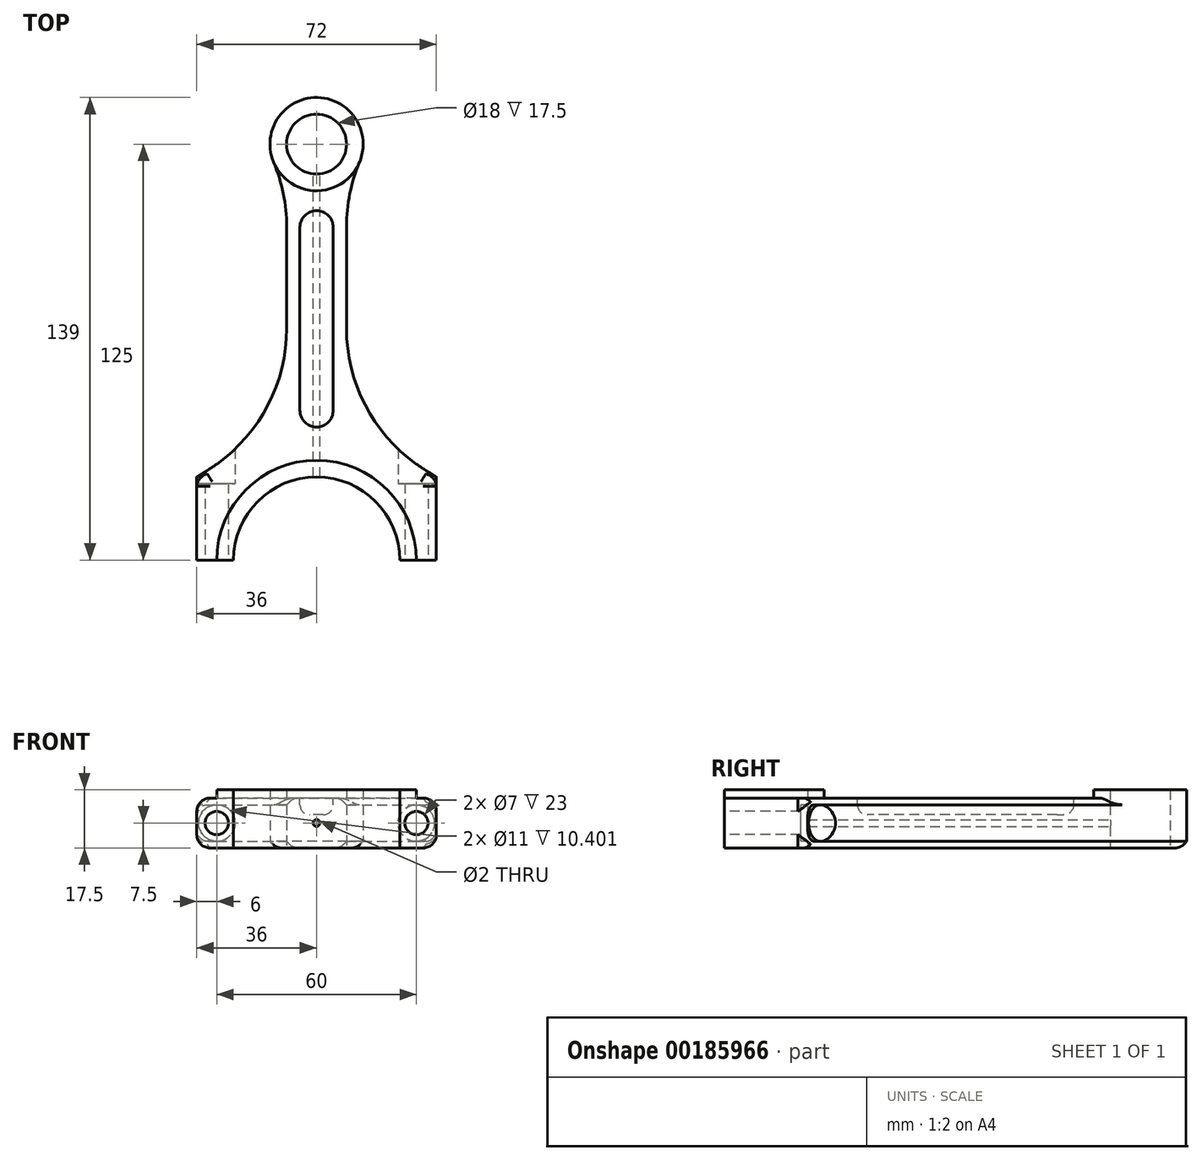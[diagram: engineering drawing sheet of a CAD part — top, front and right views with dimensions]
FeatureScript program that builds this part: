
annotation { "Feature Type Name" : "Feature", "Feature Type Description" : "" }
export const myFeature = defineFeature(function(context is Context, id is Id, definition is map)
    precondition{}
    {
        {
            var Q0;
            Q0=qCreatedBy(makeId("Top.planeOp"),FACE);
            var sketch = newSketch(context, id + "F0", { "sketchPlane" : qUnion([Q0])});
            skLineSegment(sketch, "E0", {"start": v(25, 0) * mm, "end": v(36, 0) * mm});
            skLineSegment(sketch, "E1", {"start": v(36, 0) * mm, "end": v(36, 25) * mm});
            skLineSegment(sketch, "E2", {"start": v(36, 25) * mm, "end": v(32.5, 27.19) * mm});
            skArc(sketch, "E3", {"start": v(32.5, 27.19) * mm, "mid": v(15.26, 45.35) * mm, "end": v(9, 69.59) * mm});
            skLineSegment(sketch, "E4", {"start": v(9, 69.59) * mm, "end": v(9, 100.2) * mm});
            skArc(sketch, "E5", {"start": v(9, 100.2) * mm, "mid": v(9.98, 110.08) * mm, "end": v(12.9, 119.57) * mm});
            skArc(sketch, "E6", {"start": v(12.9, 119.57) * mm, "mid": v(11.66, 132.75) * mm, "end": v(0, 139) * mm});
            skLineSegment(sketch, "E7", {"start": v(0, -25) * mm, "end": v(0, 183.63) * mm, "construction": true});
            skArc(sketch, "E8", {"start": v(25, 0) * mm, "mid": v(17.68, 17.68) * mm, "end": v(0, 25) * mm});
            skArc(sketch, "E9", {"start": v(0, 116) * mm, "mid": v(9, 125) * mm, "end": v(0, 134) * mm});
            skLineSegment(sketch, "E10.MirrorCS", {"start": v(-36, 25) * mm, "end": v(-32.5, 27.19) * mm});
            skLineSegment(sketch, "E11.MirrorCS", {"start": v(-36, 0) * mm, "end": v(-36, 25) * mm});
            skArc(sketch, "E12.MirrorCS", {"start": v(0, 116) * mm, "mid": v(-9, 125) * mm, "end": v(0, 134) * mm});
            skArc(sketch, "E13.MirrorCS", {"start": v(-25, 0) * mm, "mid": v(-17.68, 17.68) * mm, "end": v(0, 25) * mm});
            skArc(sketch, "E14.MirrorCS", {"start": v(-32.5, 27.19) * mm, "mid": v(-15.26, 45.35) * mm, "end": v(-9, 69.59) * mm});
            skLineSegment(sketch, "E15.MirrorCS", {"start": v(-25, 0) * mm, "end": v(-36, 0) * mm});
            skLineSegment(sketch, "E16.MirrorCS", {"start": v(-9, 69.59) * mm, "end": v(-9, 100.2) * mm});
            skArc(sketch, "E17.MirrorCS", {"start": v(-9, 100.2) * mm, "mid": v(-9.98, 110.08) * mm, "end": v(-12.9, 119.57) * mm});
            skArc(sketch, "E18.MirrorCS", {"start": v(-12.9, 119.57) * mm, "mid": v(-11.66, 132.75) * mm, "end": v(0, 139) * mm});
            skSolve(sketch);
        }
        {
            var Q0;
            Q0 = qSketchRegion(id + "F0", true);
            extrude(context, id + "F1", {"entities" : qUnion([Q0]), "depth" : 15 * mm, "symmetric" : true});
        }
        {
            var Q0;
            Q0=makeQuery(id+"F1.opExtrude","CAP_FACE",FACE,{"disambiguationData":[OSD([sQuery(id+"F0.wireOp",EDGE,"E0"),sQuery(id+"F0.wireOp",EDGE,"E1"),sQuery(id+"F0.wireOp",EDGE,"E2"),sQuery(id+"F0.wireOp",EDGE,"E3"),sQuery(id+"F0.wireOp",EDGE,"E4"),sQuery(id+"F0.wireOp",EDGE,"E5"),sQuery(id+"F0.wireOp",EDGE,"E6"),sQuery(id+"F0.wireOp",EDGE,"E8"),sQuery(id+"F0.wireOp",EDGE,"E9"),sQuery(id+"F0.wireOp",EDGE,"E10.MirrorCS"),sQuery(id+"F0.wireOp",EDGE,"E11.MirrorCS"),sQuery(id+"F0.wireOp",EDGE,"E12.MirrorCS"),sQuery(id+"F0.wireOp",EDGE,"E13.MirrorCS"),sQuery(id+"F0.wireOp",EDGE,"E14.MirrorCS"),sQuery(id+"F0.wireOp",EDGE,"E15.MirrorCS"),sQuery(id+"F0.wireOp",EDGE,"E16.MirrorCS"),sQuery(id+"F0.wireOp",EDGE,"E17.MirrorCS"),sQuery(id+"F0.wireOp",EDGE,"E18.MirrorCS")])],"isStart":false});
            var sketch = newSketch(context, id + "F2", { "sketchPlane" : qUnion([Q0])});
            skArc(sketch, "E19", {"start": v(30, 0) * mm, "mid": v(0, 30) * mm, "end": v(-30, 0) * mm});
            skCircle(sketch, "E20", {"center": v(0, 125) * mm, "radius": 14 * mm});
            skLineSegment(sketch, "E21", {"start": v(-30, 0) * mm, "end": v(30, 0) * mm});
            skSolve(sketch);
        }
        {
            var Q0;
            Q0=makeQuery(id+"F2.imprint","IMPRINT",FACE,{"disambiguationData":[TD([[makeQuery(id+"F2.imprint","IMPRINT",EDGE,{"derivedFrom":makeQuery(id+"F1.opExtrude","CAP_EDGE",EDGE,{"disambiguationData":[OSD([sQuery(id+"F0.wireOp",EDGE,"E9"),sQuery(id+"F0.wireOp",EDGE,"E12.MirrorCS")])],"isStart":false})}),-1.0]])]});
            var Q1;
            {var subQ0=sQuery(id+"F2.wireOp",EDGE,"E19");Q1=makeQuery(id+"F2.imprint","IMPRINT",FACE,{"disambiguationData":[TD([[makeQuery(id+"F2.imprint","IMPRINT",EDGE,{"derivedFrom":subQ0}),1.0]])]});}
            extrude(context, id + "F3", {"entities" : qUnion([Q0, Q1]), "operationType" : NewBodyOperationType.ADD, "depth" : 2.5 * mm});
        }
        {
            var Q0;
            Q0=makeQuery(id+"F1.opExtrude","CAP_FACE",FACE,{"disambiguationData":[OSD([sQuery(id+"F0.wireOp",EDGE,"E0"),sQuery(id+"F0.wireOp",EDGE,"E1"),sQuery(id+"F0.wireOp",EDGE,"E2"),sQuery(id+"F0.wireOp",EDGE,"E3"),sQuery(id+"F0.wireOp",EDGE,"E4"),sQuery(id+"F0.wireOp",EDGE,"E5"),sQuery(id+"F0.wireOp",EDGE,"E6"),sQuery(id+"F0.wireOp",EDGE,"E8"),sQuery(id+"F0.wireOp",EDGE,"E9"),sQuery(id+"F0.wireOp",EDGE,"E10.MirrorCS"),sQuery(id+"F0.wireOp",EDGE,"E11.MirrorCS"),sQuery(id+"F0.wireOp",EDGE,"E12.MirrorCS"),sQuery(id+"F0.wireOp",EDGE,"E13.MirrorCS"),sQuery(id+"F0.wireOp",EDGE,"E14.MirrorCS"),sQuery(id+"F0.wireOp",EDGE,"E15.MirrorCS"),sQuery(id+"F0.wireOp",EDGE,"E16.MirrorCS"),sQuery(id+"F0.wireOp",EDGE,"E17.MirrorCS"),sQuery(id+"F0.wireOp",EDGE,"E18.MirrorCS")])],"isStart":false});
            var sketch = newSketch(context, id + "F4", { "sketchPlane" : qUnion([Q0])});
            skLineSegment(sketch, "E22.left", {"start": v(5, 100) * mm, "end": v(5, 45) * mm});
            skLineSegment(sketch, "E22.right", {"start": v(-5, 100) * mm, "end": v(-5, 45) * mm});
            skPoint(sketch, "E22.middle", {"position": v(0, 72.5) * mm});
            skArc(sketch, "E23", {"start": v(-5, 100) * mm, "mid": v(0, 105) * mm, "end": v(5, 100) * mm});
            skArc(sketch, "E24", {"start": v(-5, 45) * mm, "mid": v(0, 40) * mm, "end": v(5, 45) * mm});
            skSolve(sketch);
        }
        {
            var Q0;
            Q0 = qSketchRegion(id + "F4", true);
            extrude(context, id + "F5", {"entities" : qUnion([Q0]), "operationType" : NewBodyOperationType.REMOVE, "oppositeDirection" : true, "depth" : 5 * mm});
        }
        {
            var Q0;
            Q0=makeQuery(id+"F1.opExtrude","CAP_EDGE",EDGE,{"disambiguationData":[OSD([sQuery(id+"F0.wireOp",EDGE,"E3")])],"isStart":false});
            var Q1;
            Q1=makeQuery(id+"F1.opExtrude","CAP_EDGE",EDGE,{"disambiguationData":[OSD([sQuery(id+"F0.wireOp",EDGE,"E3")])],"isStart":true});
            var Q2;
            Q2=makeQuery(id+"F1.opExtrude","CAP_EDGE",EDGE,{"disambiguationData":[OSD([sQuery(id+"F0.wireOp",EDGE,"E14.MirrorCS")])],"isStart":false});
            var Q3;
            Q3=makeQuery(id+"F1.opExtrude","CAP_EDGE",EDGE,{"disambiguationData":[OSD([sQuery(id+"F0.wireOp",EDGE,"E14.MirrorCS")])],"isStart":true});
            chamfer(context, id + "F6", {"entities" : qUnion([Q0, Q1, Q2, Q3]), "width" : 2 * mm, "tangentPropagation" : true});
        }
        {
            var Q0;
            {var subQ0=sQuery(id+"F2.wireOp",EDGE,"E21");var subQ1=sQuery(id+"F0.wireOp",EDGE,"E15.MirrorCS");var subQ2=makeQuery(id+"F2.imprint","IMPRINT",EDGE,{"disambiguationData":[TD([[makeQuery(id+"F2.imprint","INTERSECT",VERTEX,{"derivedFrom":[makeQuery(id+"F1.opExtrude","CAP_EDGE",EDGE,{"disambiguationData":[OSD([subQ1])],"isStart":false}),sQuery(id+"F2.wireOp",EDGE,"E19"),subQ0]}),1.0]])],"derivedFrom":subQ0});Q0=makeQuery(id+"FnDwNdTiISAMKlj_1.1.F3.boolean.opBoolean","MERGE",FACE,{"derivedFrom":[makeQuery(id+"F3.boolean.opBoolean","MERGE",FACE,{"derivedFrom":[makeQuery(id+"F1.opExtrude","SWEPT_FACE",FACE,{"disambiguationData":[OSD([subQ1])]}),makeQuery(id+"F3.opExtrude","SWEPT_FACE",FACE,{"disambiguationData":[OSD([subQ0]),TDD([subQ2])]})]}),makeQuery(id+"FnDwNdTiISAMKlj_1.1.F3.opExtrude","SWEPT_FACE",FACE,{"disambiguationData":[OSD([subQ0]),TDD([subQ2])]})]});}
            cPlane(context, id + "F7", {"entities" : qUnion([Q0]), "cplaneType" : CPlaneType.OFFSET, "offset" : 25 * mm, "oppositeDirection" : true, "width" : 150 * mm, "height" : 150 * mm});
        }
        {
            var Q0;
            Q0=qCreatedBy(id+"F7.planeOp",FACE);
            var sketch = newSketch(context, id + "F8", { "sketchPlane" : qUnion([Q0])});
            skPoint(sketch, "E25", {"position": v(-30, 0) * mm});
            skLineSegment(sketch, "E26", {"start": v(0, 28.75) * mm, "end": v(0, -30.74) * mm, "construction": true});
            skPoint(sketch, "E27.MirrorP", {"position": v(30, 0) * mm});
            skSolve(sketch);
        }
        {
            var Q0;
            Q0=sQuery(id+"F8.wireOp",VERTEX,"E27.MirrorP");
            var Q1;
            Q1=sQuery(id+"F8.wireOp",VERTEX,"E25");
            var Q2;
            Q2=makeQuery(id+"F1.opExtrude","SWEPT_BODY",BODY,{"disambiguationData":[OSD([sQuery(id+"F0.wireOp",EDGE,"E0"),sQuery(id+"F0.wireOp",EDGE,"E1"),sQuery(id+"F0.wireOp",EDGE,"E2"),sQuery(id+"F0.wireOp",EDGE,"E3"),sQuery(id+"F0.wireOp",EDGE,"E4"),sQuery(id+"F0.wireOp",EDGE,"E5"),sQuery(id+"F0.wireOp",EDGE,"E6"),sQuery(id+"F0.wireOp",EDGE,"E8"),sQuery(id+"F0.wireOp",EDGE,"E9"),sQuery(id+"F0.wireOp",EDGE,"E10.MirrorCS"),sQuery(id+"F0.wireOp",EDGE,"E11.MirrorCS"),sQuery(id+"F0.wireOp",EDGE,"E12.MirrorCS"),sQuery(id+"F0.wireOp",EDGE,"E13.MirrorCS"),sQuery(id+"F0.wireOp",EDGE,"E14.MirrorCS"),sQuery(id+"F0.wireOp",EDGE,"E15.MirrorCS"),sQuery(id+"F0.wireOp",EDGE,"E16.MirrorCS"),sQuery(id+"F0.wireOp",EDGE,"E17.MirrorCS"),sQuery(id+"F0.wireOp",EDGE,"E18.MirrorCS")])]});
            hole(context, id + "F9", {"style" : HoleStyle.C_BORE, "endStyle" : HoleEndStyle.THROUGH, "oppositeDirection" : true, "holeDiameter" : 7 * mm, "cBoreDiameter" : 11 * mm, "cBoreDepth" : 2 * mm, "locations" : qUnion([Q0, Q1]), "scope" : qUnion([Q2]), "isTappedThrough" : true, "startStyle" : HoleStartStyle.SKETCH});
        }
        {
            var Q0;
            Q0=qCreatedBy(id+"F7.planeOp",FACE);
            var sketch = newSketch(context, id + "F10", { "sketchPlane" : qUnion([Q0])});
            skCircle(sketch, "E28", {"center": v(-30, 0) * mm, "radius": 5.5 * mm});
            skCircle(sketch, "E29", {"center": v(30, 0) * mm, "radius": 5.5 * mm});
            skSolve(sketch);
        }
        {
            var Q0;
            Q0 = qSketchRegion(id + "F10", true);
            extrude(context, id + "F11", {"entities" : qUnion([Q0]), "operationType" : NewBodyOperationType.REMOVE, "oppositeDirection" : true, "depth" : 25 * mm});
        }
        {
            var Q0;
            Q0=makeQuery(id+"F9rkkF7bLStw4Ax_1.1.F5.boolean.opBoolean","COPY",EDGE,{"derivedFrom":makeQuery(id+"F9rkkF7bLStw4Ax_1.1.F5.opExtrude","CAP_EDGE",EDGE,{"disambiguationData":[OSD([sQuery(id+"F4.wireOp",EDGE,"E22.right")])],"isStart":false})});
            var Q1;
            Q1=makeQuery(id+"FnDwNdTiISAMKlj_1.1.F3.opExtrude","CAP_EDGE",EDGE,{"disambiguationData":[OSD([sQuery(id+"F2.wireOp",EDGE,"E19")])],"isStart":true});
            var Q2;
            Q2=makeQuery(id+"F3.opExtrude","CAP_EDGE",EDGE,{"disambiguationData":[OSD([sQuery(id+"F2.wireOp",EDGE,"E19")])],"isStart":true});
            var Q3;
            Q3=makeQuery(id+"F5.boolean.opBoolean","COPY",EDGE,{"derivedFrom":makeQuery(id+"F5.opExtrude","CAP_EDGE",EDGE,{"disambiguationData":[OSD([sQuery(id+"F4.wireOp",EDGE,"E22.right")])],"isStart":false})});
            fillet(context, id + "F12", {"entities" : qUnion([Q0, Q1, Q2, Q3]), "radius" : 3 * mm, "tangentPropagation" : true, "allowEdgeOverflow" : false});
        }
        {
            var Q0;
            Q0=makeQuery(id+"F6.opChamfer","BLEND_EDGE",EDGE,{"blendedFrom":[makeQuery(id+"F1.opExtrude","CAP_EDGE",EDGE,{"disambiguationData":[OSD([sQuery(id+"F0.wireOp",EDGE,"E2")])],"isStart":true}),makeQuery(id+"F1.opExtrude","SWEPT_FACE",FACE,{"disambiguationData":[OSD([sQuery(id+"F0.wireOp",EDGE,"E1")])]})],"blendedInto":[makeQuery(id+"F1.opExtrude","SWEPT_FACE",FACE,{"disambiguationData":[OSD([sQuery(id+"F0.wireOp",EDGE,"E1")])]})]});
            var Q1;
            Q1=makeQuery(id+"F6.opChamfer","BLEND_EDGE",EDGE,{"blendedFrom":[makeQuery(id+"F1.opExtrude","CAP_EDGE",EDGE,{"disambiguationData":[OSD([sQuery(id+"F0.wireOp",EDGE,"E2")])],"isStart":false}),makeQuery(id+"F1.opExtrude","SWEPT_FACE",FACE,{"disambiguationData":[OSD([sQuery(id+"F0.wireOp",EDGE,"E1")])]})],"blendedInto":[makeQuery(id+"F1.opExtrude","SWEPT_FACE",FACE,{"disambiguationData":[OSD([sQuery(id+"F0.wireOp",EDGE,"E1")])]})]});
            var Q2;
            Q2=makeQuery(id+"F6.opChamfer","BLEND_EDGE",EDGE,{"blendedFrom":[makeQuery(id+"F1.opExtrude","CAP_EDGE",EDGE,{"disambiguationData":[OSD([sQuery(id+"F0.wireOp",EDGE,"E10.MirrorCS")])],"isStart":true}),makeQuery(id+"F1.opExtrude","SWEPT_FACE",FACE,{"disambiguationData":[OSD([sQuery(id+"F0.wireOp",EDGE,"E11.MirrorCS")])]})],"blendedInto":[makeQuery(id+"F1.opExtrude","SWEPT_FACE",FACE,{"disambiguationData":[OSD([sQuery(id+"F0.wireOp",EDGE,"E11.MirrorCS")])]})]});
            var Q3;
            Q3=makeQuery(id+"F6.opChamfer","BLEND_EDGE",EDGE,{"blendedFrom":[makeQuery(id+"F1.opExtrude","CAP_EDGE",EDGE,{"disambiguationData":[OSD([sQuery(id+"F0.wireOp",EDGE,"E10.MirrorCS")])],"isStart":false}),makeQuery(id+"F1.opExtrude","SWEPT_FACE",FACE,{"disambiguationData":[OSD([sQuery(id+"F0.wireOp",EDGE,"E11.MirrorCS")])]})],"blendedInto":[makeQuery(id+"F1.opExtrude","SWEPT_FACE",FACE,{"disambiguationData":[OSD([sQuery(id+"F0.wireOp",EDGE,"E11.MirrorCS")])]})]});
            fillet(context, id + "F13", {"entities" : qUnion([Q0, Q1, Q2, Q3]), "radius" : 5 * mm, "tangentPropagation" : true, "allowEdgeOverflow" : false});
        }
        {
            var Q0;
            {var subQ0=sQuery(id+"F0.wireOp",EDGE,"E2");var subQ1=sQuery(id+"F0.wireOp",EDGE,"E1");Q0=makeQuery(id+"F13.opFillet","BLEND_EDGE",EDGE,{"blendedFrom":[makeQuery(id+"F6.opChamfer","BLEND_EDGE",EDGE,{"blendedFrom":[makeQuery(id+"F1.opExtrude","CAP_EDGE",EDGE,{"disambiguationData":[OSD([subQ0])],"isStart":true}),makeQuery(id+"F1.opExtrude","SWEPT_FACE",FACE,{"disambiguationData":[OSD([subQ1])]})],"blendedInto":[makeQuery(id+"F1.opExtrude","SWEPT_FACE",FACE,{"disambiguationData":[OSD([subQ1])]})]}),makeQuery(id+"F1.opExtrude","CAP_FACE",FACE,{"disambiguationData":[OSD([sQuery(id+"F0.wireOp",EDGE,"E0"),subQ1,subQ0,sQuery(id+"F0.wireOp",EDGE,"E3"),sQuery(id+"F0.wireOp",EDGE,"E4"),sQuery(id+"F0.wireOp",EDGE,"E5"),sQuery(id+"F0.wireOp",EDGE,"E6"),sQuery(id+"F0.wireOp",EDGE,"E8"),sQuery(id+"F0.wireOp",EDGE,"E9"),sQuery(id+"F0.wireOp",EDGE,"E10.MirrorCS"),sQuery(id+"F0.wireOp",EDGE,"E11.MirrorCS"),sQuery(id+"F0.wireOp",EDGE,"E12.MirrorCS"),sQuery(id+"F0.wireOp",EDGE,"E13.MirrorCS"),sQuery(id+"F0.wireOp",EDGE,"E14.MirrorCS"),sQuery(id+"F0.wireOp",EDGE,"E15.MirrorCS"),sQuery(id+"F0.wireOp",EDGE,"E16.MirrorCS"),sQuery(id+"F0.wireOp",EDGE,"E17.MirrorCS"),sQuery(id+"F0.wireOp",EDGE,"E18.MirrorCS")])],"isStart":true})],"blendedInto":[makeQuery(id+"F1.opExtrude","CAP_FACE",FACE,{"disambiguationData":[OSD([sQuery(id+"F0.wireOp",EDGE,"E0"),subQ1,subQ0,sQuery(id+"F0.wireOp",EDGE,"E3"),sQuery(id+"F0.wireOp",EDGE,"E4"),sQuery(id+"F0.wireOp",EDGE,"E5"),sQuery(id+"F0.wireOp",EDGE,"E6"),sQuery(id+"F0.wireOp",EDGE,"E8"),sQuery(id+"F0.wireOp",EDGE,"E9"),sQuery(id+"F0.wireOp",EDGE,"E10.MirrorCS"),sQuery(id+"F0.wireOp",EDGE,"E11.MirrorCS"),sQuery(id+"F0.wireOp",EDGE,"E12.MirrorCS"),sQuery(id+"F0.wireOp",EDGE,"E13.MirrorCS"),sQuery(id+"F0.wireOp",EDGE,"E14.MirrorCS"),sQuery(id+"F0.wireOp",EDGE,"E15.MirrorCS"),sQuery(id+"F0.wireOp",EDGE,"E16.MirrorCS"),sQuery(id+"F0.wireOp",EDGE,"E17.MirrorCS"),sQuery(id+"F0.wireOp",EDGE,"E18.MirrorCS")])],"isStart":true})]});}
            var Q1;
            {var subQ0=sQuery(id+"F0.wireOp",EDGE,"E11.MirrorCS");var subQ1=sQuery(id+"F0.wireOp",EDGE,"E10.MirrorCS");Q1=makeQuery(id+"F13.opFillet","BLEND_EDGE",EDGE,{"blendedFrom":[makeQuery(id+"F6.opChamfer","BLEND_EDGE",EDGE,{"blendedFrom":[makeQuery(id+"F1.opExtrude","CAP_EDGE",EDGE,{"disambiguationData":[OSD([subQ1])],"isStart":true}),makeQuery(id+"F1.opExtrude","SWEPT_FACE",FACE,{"disambiguationData":[OSD([subQ0])]})],"blendedInto":[makeQuery(id+"F1.opExtrude","SWEPT_FACE",FACE,{"disambiguationData":[OSD([subQ0])]})]}),makeQuery(id+"F1.opExtrude","CAP_FACE",FACE,{"disambiguationData":[OSD([sQuery(id+"F0.wireOp",EDGE,"E0"),sQuery(id+"F0.wireOp",EDGE,"E1"),sQuery(id+"F0.wireOp",EDGE,"E2"),sQuery(id+"F0.wireOp",EDGE,"E3"),sQuery(id+"F0.wireOp",EDGE,"E4"),sQuery(id+"F0.wireOp",EDGE,"E5"),sQuery(id+"F0.wireOp",EDGE,"E6"),sQuery(id+"F0.wireOp",EDGE,"E8"),sQuery(id+"F0.wireOp",EDGE,"E9"),subQ1,subQ0,sQuery(id+"F0.wireOp",EDGE,"E12.MirrorCS"),sQuery(id+"F0.wireOp",EDGE,"E13.MirrorCS"),sQuery(id+"F0.wireOp",EDGE,"E14.MirrorCS"),sQuery(id+"F0.wireOp",EDGE,"E15.MirrorCS"),sQuery(id+"F0.wireOp",EDGE,"E16.MirrorCS"),sQuery(id+"F0.wireOp",EDGE,"E17.MirrorCS"),sQuery(id+"F0.wireOp",EDGE,"E18.MirrorCS")])],"isStart":true})],"blendedInto":[makeQuery(id+"F1.opExtrude","CAP_FACE",FACE,{"disambiguationData":[OSD([sQuery(id+"F0.wireOp",EDGE,"E0"),sQuery(id+"F0.wireOp",EDGE,"E1"),sQuery(id+"F0.wireOp",EDGE,"E2"),sQuery(id+"F0.wireOp",EDGE,"E3"),sQuery(id+"F0.wireOp",EDGE,"E4"),sQuery(id+"F0.wireOp",EDGE,"E5"),sQuery(id+"F0.wireOp",EDGE,"E6"),sQuery(id+"F0.wireOp",EDGE,"E8"),sQuery(id+"F0.wireOp",EDGE,"E9"),subQ1,subQ0,sQuery(id+"F0.wireOp",EDGE,"E12.MirrorCS"),sQuery(id+"F0.wireOp",EDGE,"E13.MirrorCS"),sQuery(id+"F0.wireOp",EDGE,"E14.MirrorCS"),sQuery(id+"F0.wireOp",EDGE,"E15.MirrorCS"),sQuery(id+"F0.wireOp",EDGE,"E16.MirrorCS"),sQuery(id+"F0.wireOp",EDGE,"E17.MirrorCS"),sQuery(id+"F0.wireOp",EDGE,"E18.MirrorCS")])],"isStart":true})]});}
            var Q2;
            {var subQ0=sQuery(id+"F0.wireOp",EDGE,"E11.MirrorCS");var subQ1=sQuery(id+"F0.wireOp",EDGE,"E10.MirrorCS");Q2=makeQuery(id+"F13.opFillet","BLEND_EDGE",EDGE,{"blendedFrom":[makeQuery(id+"F6.opChamfer","BLEND_EDGE",EDGE,{"blendedFrom":[makeQuery(id+"F1.opExtrude","CAP_EDGE",EDGE,{"disambiguationData":[OSD([subQ1])],"isStart":false}),makeQuery(id+"F1.opExtrude","SWEPT_FACE",FACE,{"disambiguationData":[OSD([subQ0])]})],"blendedInto":[makeQuery(id+"F1.opExtrude","SWEPT_FACE",FACE,{"disambiguationData":[OSD([subQ0])]})]}),makeQuery(id+"F1.opExtrude","CAP_FACE",FACE,{"disambiguationData":[OSD([sQuery(id+"F0.wireOp",EDGE,"E0"),sQuery(id+"F0.wireOp",EDGE,"E1"),sQuery(id+"F0.wireOp",EDGE,"E2"),sQuery(id+"F0.wireOp",EDGE,"E3"),sQuery(id+"F0.wireOp",EDGE,"E4"),sQuery(id+"F0.wireOp",EDGE,"E5"),sQuery(id+"F0.wireOp",EDGE,"E6"),sQuery(id+"F0.wireOp",EDGE,"E8"),sQuery(id+"F0.wireOp",EDGE,"E9"),subQ1,subQ0,sQuery(id+"F0.wireOp",EDGE,"E12.MirrorCS"),sQuery(id+"F0.wireOp",EDGE,"E13.MirrorCS"),sQuery(id+"F0.wireOp",EDGE,"E14.MirrorCS"),sQuery(id+"F0.wireOp",EDGE,"E15.MirrorCS"),sQuery(id+"F0.wireOp",EDGE,"E16.MirrorCS"),sQuery(id+"F0.wireOp",EDGE,"E17.MirrorCS"),sQuery(id+"F0.wireOp",EDGE,"E18.MirrorCS")])],"isStart":false})],"blendedInto":[makeQuery(id+"F1.opExtrude","CAP_FACE",FACE,{"disambiguationData":[OSD([sQuery(id+"F0.wireOp",EDGE,"E0"),sQuery(id+"F0.wireOp",EDGE,"E1"),sQuery(id+"F0.wireOp",EDGE,"E2"),sQuery(id+"F0.wireOp",EDGE,"E3"),sQuery(id+"F0.wireOp",EDGE,"E4"),sQuery(id+"F0.wireOp",EDGE,"E5"),sQuery(id+"F0.wireOp",EDGE,"E6"),sQuery(id+"F0.wireOp",EDGE,"E8"),sQuery(id+"F0.wireOp",EDGE,"E9"),subQ1,subQ0,sQuery(id+"F0.wireOp",EDGE,"E12.MirrorCS"),sQuery(id+"F0.wireOp",EDGE,"E13.MirrorCS"),sQuery(id+"F0.wireOp",EDGE,"E14.MirrorCS"),sQuery(id+"F0.wireOp",EDGE,"E15.MirrorCS"),sQuery(id+"F0.wireOp",EDGE,"E16.MirrorCS"),sQuery(id+"F0.wireOp",EDGE,"E17.MirrorCS"),sQuery(id+"F0.wireOp",EDGE,"E18.MirrorCS")])],"isStart":false})]});}
            var Q3;
            {var subQ0=sQuery(id+"F0.wireOp",EDGE,"E2");var subQ1=sQuery(id+"F0.wireOp",EDGE,"E1");Q3=makeQuery(id+"F13.opFillet","BLEND_EDGE",EDGE,{"blendedFrom":[makeQuery(id+"F6.opChamfer","BLEND_EDGE",EDGE,{"blendedFrom":[makeQuery(id+"F1.opExtrude","CAP_EDGE",EDGE,{"disambiguationData":[OSD([subQ0])],"isStart":false}),makeQuery(id+"F1.opExtrude","SWEPT_FACE",FACE,{"disambiguationData":[OSD([subQ1])]})],"blendedInto":[makeQuery(id+"F1.opExtrude","SWEPT_FACE",FACE,{"disambiguationData":[OSD([subQ1])]})]}),makeQuery(id+"F1.opExtrude","CAP_FACE",FACE,{"disambiguationData":[OSD([sQuery(id+"F0.wireOp",EDGE,"E0"),subQ1,subQ0,sQuery(id+"F0.wireOp",EDGE,"E3"),sQuery(id+"F0.wireOp",EDGE,"E4"),sQuery(id+"F0.wireOp",EDGE,"E5"),sQuery(id+"F0.wireOp",EDGE,"E6"),sQuery(id+"F0.wireOp",EDGE,"E8"),sQuery(id+"F0.wireOp",EDGE,"E9"),sQuery(id+"F0.wireOp",EDGE,"E10.MirrorCS"),sQuery(id+"F0.wireOp",EDGE,"E11.MirrorCS"),sQuery(id+"F0.wireOp",EDGE,"E12.MirrorCS"),sQuery(id+"F0.wireOp",EDGE,"E13.MirrorCS"),sQuery(id+"F0.wireOp",EDGE,"E14.MirrorCS"),sQuery(id+"F0.wireOp",EDGE,"E15.MirrorCS"),sQuery(id+"F0.wireOp",EDGE,"E16.MirrorCS"),sQuery(id+"F0.wireOp",EDGE,"E17.MirrorCS"),sQuery(id+"F0.wireOp",EDGE,"E18.MirrorCS")])],"isStart":false})],"blendedInto":[makeQuery(id+"F1.opExtrude","CAP_FACE",FACE,{"disambiguationData":[OSD([sQuery(id+"F0.wireOp",EDGE,"E0"),subQ1,subQ0,sQuery(id+"F0.wireOp",EDGE,"E3"),sQuery(id+"F0.wireOp",EDGE,"E4"),sQuery(id+"F0.wireOp",EDGE,"E5"),sQuery(id+"F0.wireOp",EDGE,"E6"),sQuery(id+"F0.wireOp",EDGE,"E8"),sQuery(id+"F0.wireOp",EDGE,"E9"),sQuery(id+"F0.wireOp",EDGE,"E10.MirrorCS"),sQuery(id+"F0.wireOp",EDGE,"E11.MirrorCS"),sQuery(id+"F0.wireOp",EDGE,"E12.MirrorCS"),sQuery(id+"F0.wireOp",EDGE,"E13.MirrorCS"),sQuery(id+"F0.wireOp",EDGE,"E14.MirrorCS"),sQuery(id+"F0.wireOp",EDGE,"E15.MirrorCS"),sQuery(id+"F0.wireOp",EDGE,"E16.MirrorCS"),sQuery(id+"F0.wireOp",EDGE,"E17.MirrorCS"),sQuery(id+"F0.wireOp",EDGE,"E18.MirrorCS")])],"isStart":false})]});}
            fillet(context, id + "F14", {"entities" : qUnion([Q0, Q1, Q2, Q3]), "radius" : 4 * mm, "tangentPropagation" : true, "allowEdgeOverflow" : false});
        }
        {
            var Q0;
            {var subQ0=sQuery(id+"F2.wireOp",EDGE,"E19");Q0=makeQuery(id+"F12.opFillet","BLEND_EDGE",EDGE,{"blendedFrom":[makeQuery(id+"F3.opExtrude","CAP_EDGE",EDGE,{"disambiguationData":[OSD([subQ0])],"isStart":true}),makeQuery(id+"F3.opExtrude","CAP_FACE",FACE,{"disambiguationData":[OSD([sQuery(id+"F0.wireOp",EDGE,"E8"),sQuery(id+"F0.wireOp",EDGE,"E13.MirrorCS"),subQ0,sQuery(id+"F2.wireOp",EDGE,"E21")])],"isStart":false})],"blendedInto":[makeQuery(id+"F3.opExtrude","CAP_FACE",FACE,{"disambiguationData":[OSD([sQuery(id+"F0.wireOp",EDGE,"E8"),sQuery(id+"F0.wireOp",EDGE,"E13.MirrorCS"),subQ0,sQuery(id+"F2.wireOp",EDGE,"E21")])],"isStart":false})]});}
            var Q1;
            Q1=makeQuery(id+"F3.opExtrude","CAP_EDGE",EDGE,{"disambiguationData":[OSD([sQuery(id+"F0.wireOp",EDGE,"E8"),sQuery(id+"F0.wireOp",EDGE,"E13.MirrorCS")])],"isStart":false});
            var Q2;
            Q2=makeQuery(id+"FnDwNdTiISAMKlj_1.1.F3.opExtrude","CAP_EDGE",EDGE,{"disambiguationData":[OSD([sQuery(id+"F0.wireOp",EDGE,"E8"),sQuery(id+"F0.wireOp",EDGE,"E13.MirrorCS")])],"isStart":false});
            var Q3;
            {var subQ0=sQuery(id+"F2.wireOp",EDGE,"E19");Q3=makeQuery(id+"F12.opFillet","BLEND_EDGE",EDGE,{"blendedFrom":[makeQuery(id+"FnDwNdTiISAMKlj_1.1.F3.opExtrude","CAP_EDGE",EDGE,{"disambiguationData":[OSD([subQ0])],"isStart":true}),makeQuery(id+"FnDwNdTiISAMKlj_1.1.F3.opExtrude","CAP_FACE",FACE,{"disambiguationData":[OSD([sQuery(id+"F0.wireOp",EDGE,"E8"),sQuery(id+"F0.wireOp",EDGE,"E13.MirrorCS"),subQ0,sQuery(id+"F2.wireOp",EDGE,"E21")])],"isStart":false})],"blendedInto":[makeQuery(id+"FnDwNdTiISAMKlj_1.1.F3.opExtrude","CAP_FACE",FACE,{"disambiguationData":[OSD([sQuery(id+"F0.wireOp",EDGE,"E8"),sQuery(id+"F0.wireOp",EDGE,"E13.MirrorCS"),subQ0,sQuery(id+"F2.wireOp",EDGE,"E21")])],"isStart":false})]});}
            fillet(context, id + "F15", {"entities" : qUnion([Q0, Q1, Q2, Q3]), "radius" : .3 * mm, "tangentPropagation" : true, "allowEdgeOverflow" : false});
        }
        {
            var Q0;
            {var subQ0=sQuery(id+"F2.wireOp",EDGE,"E21");var subQ1=sQuery(id+"F0.wireOp",EDGE,"E15.MirrorCS");var subQ2=makeQuery(id+"F2.imprint","IMPRINT",EDGE,{"disambiguationData":[TD([[makeQuery(id+"F2.imprint","INTERSECT",VERTEX,{"derivedFrom":[makeQuery(id+"F1.opExtrude","CAP_EDGE",EDGE,{"disambiguationData":[OSD([subQ1])],"isStart":false}),sQuery(id+"F2.wireOp",EDGE,"E19"),subQ0]}),1.0]])],"derivedFrom":subQ0});Q0=makeQuery(id+"FnDwNdTiISAMKlj_1.1.F3.boolean.opBoolean","MERGE",FACE,{"derivedFrom":[makeQuery(id+"F3.boolean.opBoolean","MERGE",FACE,{"derivedFrom":[makeQuery(id+"F1.opExtrude","SWEPT_FACE",FACE,{"disambiguationData":[OSD([subQ1])]}),makeQuery(id+"F3.opExtrude","SWEPT_FACE",FACE,{"disambiguationData":[OSD([subQ0]),TDD([subQ2])]})]}),makeQuery(id+"FnDwNdTiISAMKlj_1.1.F3.opExtrude","SWEPT_FACE",FACE,{"disambiguationData":[OSD([subQ0]),TDD([subQ2])]})]});}
            cPlane(context, id + "F16", {"entities" : qUnion([Q0]), "cplaneType" : CPlaneType.OFFSET, "offset" : 125 * mm, "oppositeDirection" : true, "width" : 150 * mm, "height" : 150 * mm});
        }
        {
            var Q0;
            Q0=qCreatedBy(id+"F16.planeOp",FACE);
            var sketch = newSketch(context, id + "F17", { "sketchPlane" : qUnion([Q0])});
            skCircle(sketch, "E30", {"center": v(0, 0) * mm, "radius": 1 * mm});
            skSolve(sketch);
        }
        {
            var Q0;
            Q0 = qSketchRegion(id + "F17", true);
            extrude(context, id + "F18", {"entities" : qUnion([Q0]), "operationType" : NewBodyOperationType.REMOVE, "endBound" : BoundingType.THROUGH_ALL, "depth" : 25 * mm});
        }
    });
